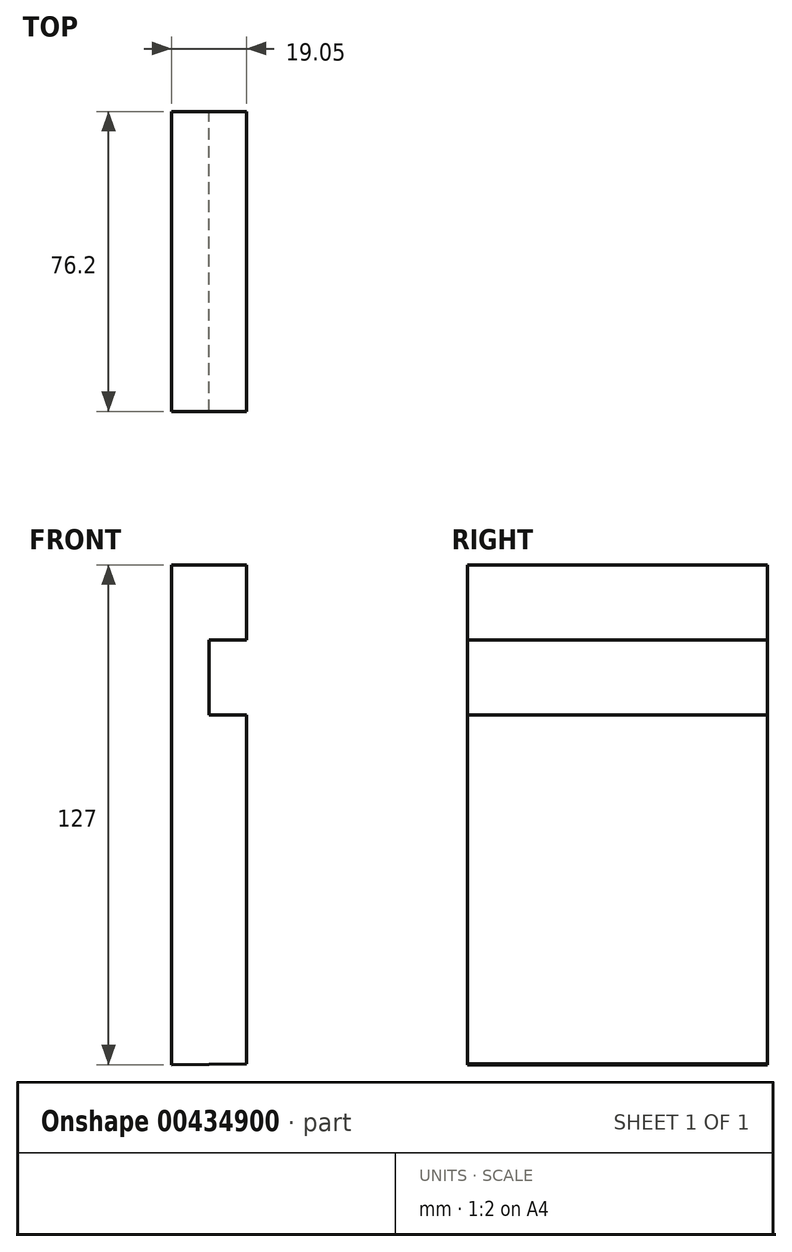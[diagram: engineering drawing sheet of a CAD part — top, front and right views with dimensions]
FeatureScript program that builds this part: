
annotation { "Feature Type Name" : "Feature", "Feature Type Description" : "" }
export const myFeature = defineFeature(function(context is Context, id is Id, definition is map)
    precondition{}
    {
        {
            var Q0;
            Q0=qCreatedBy(makeId("Front.planeOp"),FACE);
            var sketch = newSketch(context, id + "F0", { "sketchPlane" : qUnion([Q0])});
            skLineSegment(sketch, "E0", {"start": v(-55.57, -65.69) * mm, "end": v(-55.57, 61.31) * mm});
            skLineSegment(sketch, "E1", {"start": v(-55.57, 61.31) * mm, "end": v(-36.52, 61.31) * mm});
            skLineSegment(sketch, "E2", {"start": v(-36.52, 61.31) * mm, "end": v(-36.52, 42.26) * mm});
            skLineSegment(sketch, "E3", {"start": v(-36.52, 42.26) * mm, "end": v(-46.04, 42.26) * mm});
            skLineSegment(sketch, "E4", {"start": v(-46.04, 42.26) * mm, "end": v(-46.04, 23.21) * mm});
            skLineSegment(sketch, "E5", {"start": v(-46.04, 23.21) * mm, "end": v(-36.52, 23.21) * mm});
            skLineSegment(sketch, "E6", {"start": v(-36.52, 23.21) * mm, "end": v(-36.52, -65.5) * mm});
            skLineSegment(sketch, "E7", {"start": v(-36.52, -65.5) * mm, "end": v(-55.57, -65.69) * mm});
            skSolve(sketch);
        }
        {
            var Q0;
            Q0 = qSketchRegion(id + "F0", true);
            extrude(context, id + "F1", {"entities" : qUnion([Q0]), "depth" : 76.2 * mm});
        }
    });
